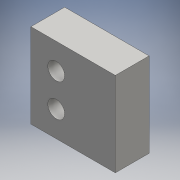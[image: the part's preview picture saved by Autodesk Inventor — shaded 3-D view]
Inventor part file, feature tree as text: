
AUTODESK INVENTOR PART (.ipt)
format: ipt  version: 2016 (Build 200138000, 138)  size: 93,184 bytes
history: native  units: mm
features: extrude x1, sketch x1
ambient origin geometry x8: Origin, YZ Plane, XZ Plane, XY Plane, X Axis, Y Axis, Z Axis, Center Point
bodies: Solid1 (feature_tree)
feature tree (2):
  extrude  "Extrusion1"  Depth=20.0mm
  sketch  "Sketch1"  dims[d0=20.0mm d1=20.0mm d2=4.0mm d3=4.0mm d4=7.8mm d5=6.1mm d6=6.0mm d7=6.0mm d8=8.0mm d9=0.0mm]
